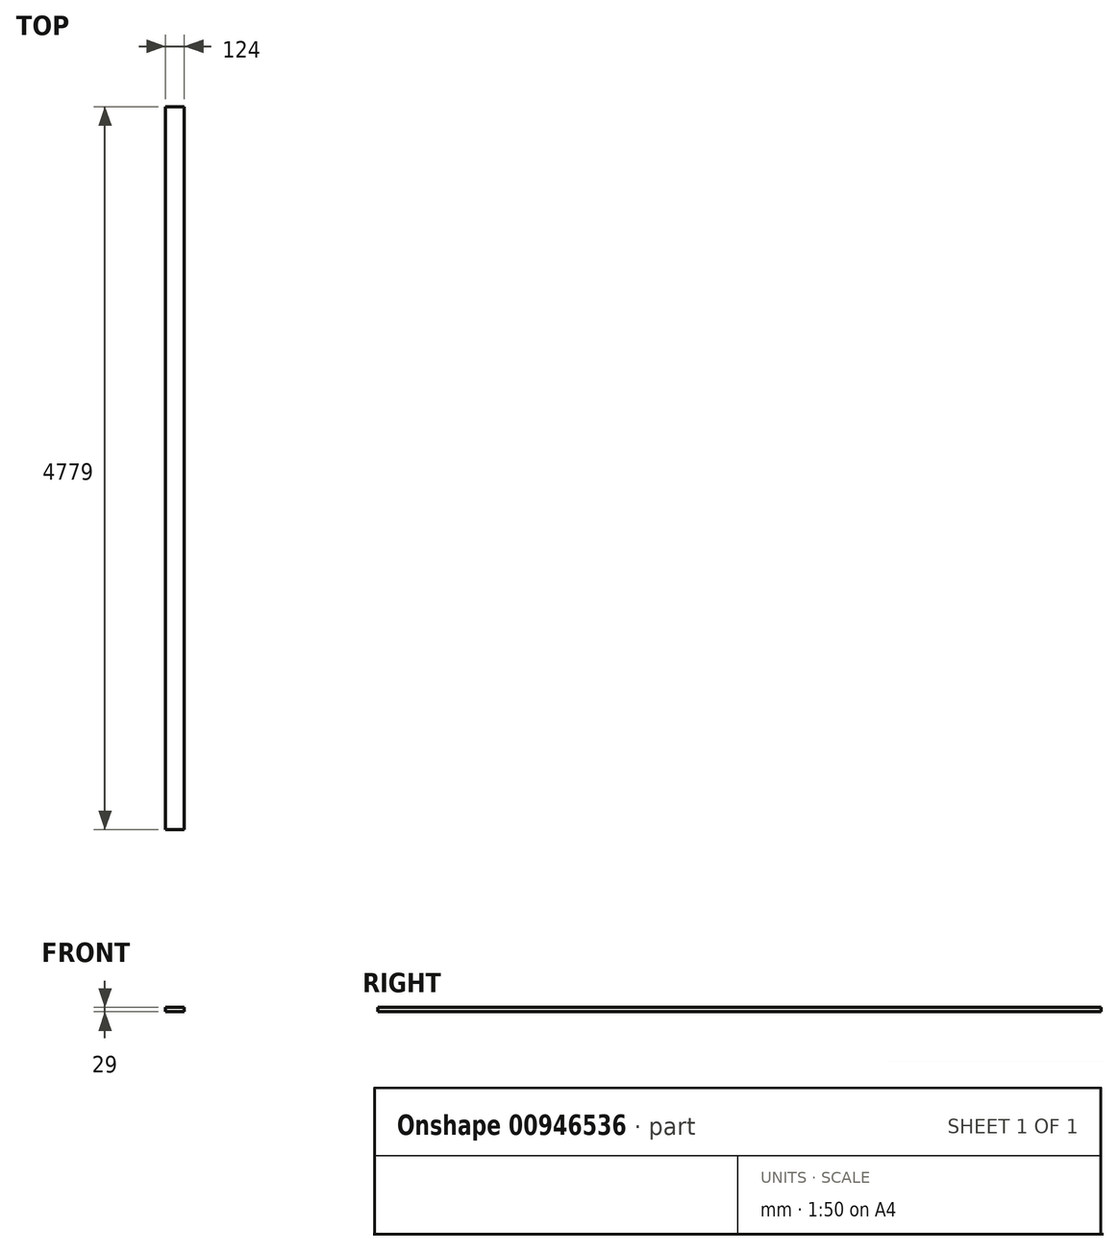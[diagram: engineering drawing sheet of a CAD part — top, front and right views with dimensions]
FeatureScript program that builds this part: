
annotation { "Feature Type Name" : "Feature", "Feature Type Description" : "" }
export const myFeature = defineFeature(function(context is Context, id is Id, definition is map)
    precondition{}
    {
        {
            var Q0;
            Q0=qCreatedBy(makeId("Front.planeOp"),FACE);
            var sketch = newSketch(context, id + "F0", { "sketchPlane" : qUnion([Q0])});
            skLineSegment(sketch, "E0.bottom", {"start": v(0, 0) * mm, "end": v(124, 0) * mm});
            skLineSegment(sketch, "E0.top", {"start": v(0, 29) * mm, "end": v(124, 29) * mm});
            skLineSegment(sketch, "E0.left", {"start": v(0, 0) * mm, "end": v(0, 29) * mm});
            skLineSegment(sketch, "E0.right", {"start": v(124, 0) * mm, "end": v(124, 29) * mm});
            skSolve(sketch);
        }
        {
            var Q0;
            Q0=qSketchRegion(id+"F0",true);
            extrude(context, id + "F1", {"entities" : qUnion([Q0]), "depth" : 4779 * mm, "offsetDistance" : 25 * mm});
        }
    });
